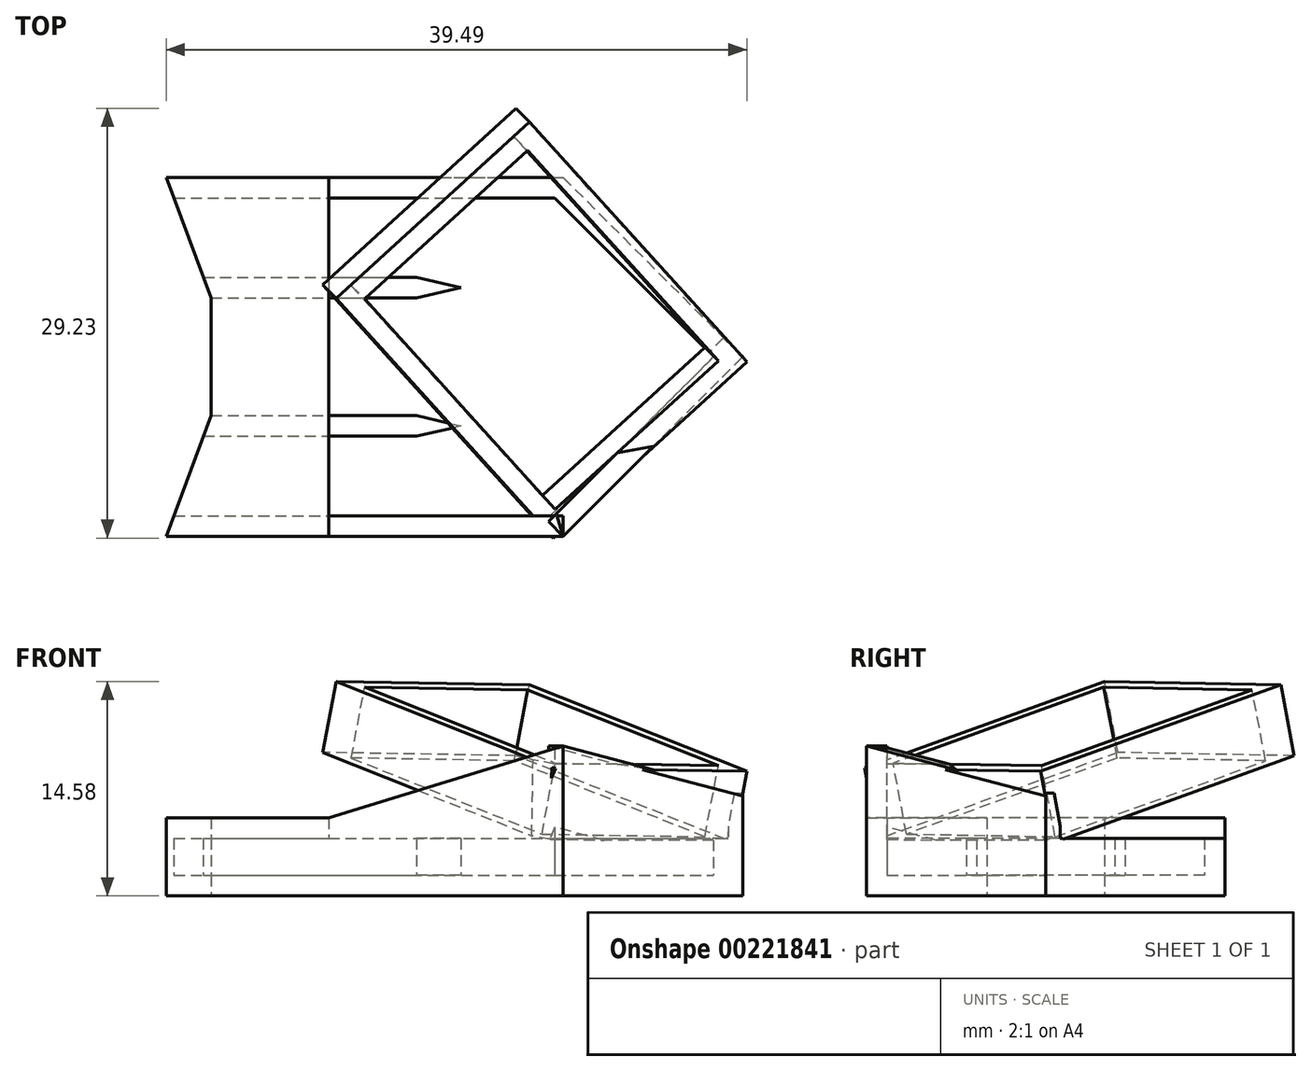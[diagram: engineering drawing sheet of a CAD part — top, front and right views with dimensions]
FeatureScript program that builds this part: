
annotation { "Feature Type Name" : "Feature", "Feature Type Description" : "" }
export const myFeature = defineFeature(function(context is Context, id is Id, definition is map)
    precondition{}
    {
        {
            var Q0;
            Q0=qCreatedBy(makeId("Top.planeOp"),FACE);
            var sketch = newSketch(context, id + "F0", { "sketchPlane" : qUnion([Q0])});
            skLineSegment(sketch, "E0", {"start": v(0, 12.2) * mm, "end": v(3.03, 4) * mm});
            skLineSegment(sketch, "E1", {"start": v(3.03, 4) * mm, "end": v(3.03, 0) * mm});
            skLineSegment(sketch, "E2", {"start": v(0, 12.2) * mm, "end": v(27, 12.2) * mm});
            skLineSegment(sketch, "E3", {"start": v(27, 12.2) * mm, "end": v(39.2, 0) * mm});
            skLineSegment(sketch, "E4.MirrorCS", {"start": v(0, -12.2) * mm, "end": v(3.03, -4) * mm});
            skLineSegment(sketch, "E5.MirrorCS", {"start": v(3.03, -4) * mm, "end": v(3.03, 0) * mm});
            skLineSegment(sketch, "E6.MirrorCS", {"start": v(27, -12.2) * mm, "end": v(39.2, 0) * mm});
            skLineSegment(sketch, "E7.MirrorCS", {"start": v(0, -12.2) * mm, "end": v(27, -12.2) * mm});
            skSolve(sketch);
        }
        {
            var Q0;
            Q0=makeQuery(id+"F0.imprint","IMPRINT",FACE,{"disambiguationData":[TD([[makeQuery(id+"F0.imprint","IMPRINT",EDGE,{"derivedFrom":sQuery(id+"F0.wireOp",EDGE,"E0")}),1.0]])]});
            extrude(context, id + "F1", {"entities" : qUnion([Q0]), "depth" : 1.4 * mm});
        }
        {
            var Q0;
            Q0=makeQuery(id+"F1.opExtrude","CAP_FACE",FACE,{"disambiguationData":[OSD([sQuery(id+"F0.wireOp",EDGE,"E0"),sQuery(id+"F0.wireOp",EDGE,"E1"),sQuery(id+"F0.wireOp",EDGE,"E2"),sQuery(id+"F0.wireOp",EDGE,"E3"),sQuery(id+"F0.wireOp",EDGE,"E4.MirrorCS"),sQuery(id+"F0.wireOp",EDGE,"E5.MirrorCS"),sQuery(id+"F0.wireOp",EDGE,"E6.MirrorCS"),sQuery(id+"F0.wireOp",EDGE,"E7.MirrorCS")])],"isStart":false});
            var sketch = newSketch(context, id + "F2", { "sketchPlane" : qUnion([Q0])});
            skLineSegment(sketch, "E8.0", {"start": v(0, -12.2) * mm, "end": v(3.03, -4) * mm});
            skLineSegment(sketch, "E9.0", {"start": v(0, 12.2) * mm, "end": v(3.03, 4) * mm});
            skLineSegment(sketch, "E10", {"start": v(3.03, -4) * mm, "end": v(17.03, -4) * mm});
            skLineSegment(sketch, "E11", {"start": v(2.51, -5.4) * mm, "end": v(17.03, -5.4) * mm});
            skLineSegment(sketch, "E12", {"start": v(17.03, -4) * mm, "end": v(17.03, -5.4) * mm, "construction": true});
            skLineSegment(sketch, "E13", {"start": v(17.03, -4) * mm, "end": v(20.03, -4.7) * mm});
            skPoint(sketch, "E13.endSnap0", {"position": v(17.03, -4.7) * mm});
            skLineSegment(sketch, "E14", {"start": v(20.03, -4.7) * mm, "end": v(17.03, -5.4) * mm});
            skLineSegment(sketch, "E15.MirrorCS", {"start": v(17.03, 4) * mm, "end": v(20.03, 4.7) * mm});
            skLineSegment(sketch, "E16.MirrorCS", {"start": v(20.03, 4.7) * mm, "end": v(17.03, 5.4) * mm});
            skLineSegment(sketch, "E17.MirrorCS", {"start": v(2.51, 5.4) * mm, "end": v(17.03, 5.4) * mm});
            skLineSegment(sketch, "E18.MirrorCS", {"start": v(3.03, 4) * mm, "end": v(17.03, 4) * mm});
            skLineSegment(sketch, "E19.0", {"start": v(0, -12.2) * mm, "end": v(27, -12.2) * mm});
            skLineSegment(sketch, "E20.0", {"start": v(27, -12.2) * mm, "end": v(39.2, 0) * mm});
            skLineSegment(sketch, "E21", {"start": v(0.52, -10.8) * mm, "end": v(26.42, -10.8) * mm});
            skLineSegment(sketch, "E22", {"start": v(26.42, -10.8) * mm, "end": v(37.22, 0) * mm});
            skLineSegment(sketch, "E23.MirrorCS", {"start": v(26.42, 10.8) * mm, "end": v(37.22, 0) * mm});
            skLineSegment(sketch, "E24.MirrorCS", {"start": v(0.52, 10.8) * mm, "end": v(26.42, 10.8) * mm});
            skLineSegment(sketch, "E25.MirrorCS", {"start": v(0, 12.2) * mm, "end": v(27, 12.2) * mm});
            skLineSegment(sketch, "E26.MirrorCS", {"start": v(27, 12.2) * mm, "end": v(39.2, 0) * mm});
            skSolve(sketch);
        }
        {
            var Q0;
            Q0 = qSketchRegion(id + "F2", true);
            extrude(context, id + "F3", {"entities" : qUnion([Q0]), "operationType" : NewBodyOperationType.ADD, "depth" : 2.5 * mm});
        }
        {
            var Q0;
            Q0=makeQuery(id+"F3.opExtrude","CAP_FACE",FACE,{"disambiguationData":[OSD([sQuery(id+"F2.wireOp",EDGE,"E8.0"),sQuery(id+"F2.wireOp",EDGE,"E10"),sQuery(id+"F2.wireOp",EDGE,"E11"),sQuery(id+"F2.wireOp",EDGE,"E13"),sQuery(id+"F2.wireOp",EDGE,"E14")])],"isStart":false});
            var sketch = newSketch(context, id + "F4", { "sketchPlane" : qUnion([Q0])});
            skLineSegment(sketch, "E27.0", {"start": v(0, 12.2) * mm, "end": v(2.51, 5.4) * mm});
            skLineSegment(sketch, "E28.0", {"start": v(0, 12.2) * mm, "end": v(11.03, 12.2) * mm});
            skLineSegment(sketch, "E29.0.0", {"start": v(2.51, 5.4) * mm, "end": v(3.03, 4) * mm});
            skLineSegment(sketch, "E30.0", {"start": v(3.03, 4) * mm, "end": v(3.03, -4) * mm});
            skLineSegment(sketch, "E31.0", {"start": v(0, -12.2) * mm, "end": v(2.51, -5.4) * mm});
            skLineSegment(sketch, "E32.0", {"start": v(0, -12.2) * mm, "end": v(11.03, -12.2) * mm});
            skLineSegment(sketch, "E33", {"start": v(11.03, 12.2) * mm, "end": v(11.03, -12.2) * mm});
            skPoint(sketch, "E29.0.3.end.orphan", {"position": v(17.03, 5.4) * mm});
            skPoint(sketch, "E29.0.2.end.orphan", {"position": v(20.03, 4.7) * mm});
            skPoint(sketch, "E34.orphan", {"position": v(17.03, 4) * mm});
            skPoint(sketch, "E35.0.3.end.orphan", {"position": v(17.03, -4) * mm});
            skPoint(sketch, "E35.0.2.end.orphan", {"position": v(20.03, -4.7) * mm});
            skPoint(sketch, "E35.0.2.start.orphan", {"position": v(17.03, -5.4) * mm});
            skLineSegment(sketch, "E36", {"start": v(3.03, -4) * mm, "end": v(2.51, -5.4) * mm});
            skSolve(sketch);
        }
        {
            var Q0;
            Q0=makeQuery(id+"F4.imprint","IMPRINT",FACE,{"disambiguationData":[TD([[makeQuery(id+"F4.imprint","IMPRINT",EDGE,{"derivedFrom":sQuery(id+"F4.wireOp",EDGE,"E27.0")}),1.0]])]});
            var Q1;
            {var subQ5=sQuery(id+"F4.wireOp",EDGE,"E36");Q1=makeQuery(id+"F4.imprint","IMPRINT",FACE,{"disambiguationData":[TD([[makeQuery(id+"F4.imprint","IMPRINT",EDGE,{"derivedFrom":subQ5}),-1.0]])]});}
            var Q2;
            {var subQ0=sQuery(id+"F4.wireOp",EDGE,"E31.0");Q2=makeQuery(id+"F4.imprint","IMPRINT",FACE,{"disambiguationData":[TD([[makeQuery(id+"F4.imprint","IMPRINT",EDGE,{"derivedFrom":subQ0}),-1.0]])]});}
            extrude(context, id + "F5", {"entities" : qUnion([Q0, Q1, Q2]), "operationType" : NewBodyOperationType.ADD, "depth" : 1.4 * mm});
        }
        {
            var Q0;
            Q0=makeQuery(id+"F5.boolean.opBoolean","MERGE",FACE,{"derivedFrom":[makeQuery(id+"F3.boolean.opBoolean","MERGE",FACE,{"derivedFrom":[makeQuery(id+"F1.opExtrude","SWEPT_FACE",FACE,{"disambiguationData":[OSD([sQuery(id+"F0.wireOp",EDGE,"E7.MirrorCS")])]}),makeQuery(id+"F3.opExtrude","SWEPT_FACE",FACE,{"disambiguationData":[OSD([sQuery(id+"F2.wireOp",EDGE,"E19.0")])]})]}),makeQuery(id+"F5.opExtrude","SWEPT_FACE",FACE,{"disambiguationData":[OSD([sQuery(id+"F4.wireOp",EDGE,"E32.0")])]})]});
            var sketch = newSketch(context, id + "F6", { "sketchPlane" : qUnion([Q0])});
            skLineSegment(sketch, "E37", {"start": v(11.03, 5.3) * mm, "end": v(27, 10.18) * mm});
            skLineSegment(sketch, "E38.0", {"start": v(11.03, 5.3) * mm, "end": v(11.03, 3.9) * mm});
            skLineSegment(sketch, "E39.0", {"start": v(11.03, 3.9) * mm, "end": v(27, 3.9) * mm});
            skLineSegment(sketch, "E40", {"start": v(27, 10.18) * mm, "end": v(27, 3.9) * mm});
            skSolve(sketch);
        }
        {
            var Q0;
            Q0 = qSketchRegion(id + "F6", true);
            var Q1;
            Q1=makeQuery(id+"F3.opExtrude","SWEPT_FACE",FACE,{"disambiguationData":[OSD([sQuery(id+"F2.wireOp",EDGE,"E21")])]});
            extrude(context, id + "F7", {"entities" : qUnion([Q0]), "operationType" : NewBodyOperationType.ADD, "endBound" : BoundingType.UP_TO_SURFACE, "oppositeDirection" : true, "endBoundEntityFace" : qUnion([Q1]), "depth" : 25 * mm});
        }
        {
            var Q0;
            Q0=makeQuery(id+"F3.boolean.opBoolean","MERGE",FACE,{"derivedFrom":[makeQuery(id+"F1.opExtrude","SWEPT_FACE",FACE,{"disambiguationData":[OSD([sQuery(id+"F0.wireOp",EDGE,"E6.MirrorCS")])]}),makeQuery(id+"F3.opExtrude","SWEPT_FACE",FACE,{"disambiguationData":[OSD([sQuery(id+"F2.wireOp",EDGE,"E20.0")])]})]});
            var sketch = newSketch(context, id + "F8", { "sketchPlane" : qUnion([Q0])});
            skLineSegment(sketch, "E41.0", {"start": v(10.47, 10.18) * mm, "end": v(10.47, 3.9) * mm});
            skLineSegment(sketch, "E42.0", {"start": v(10.47, 3.9) * mm, "end": v(27.72, 3.9) * mm});
            skLineSegment(sketch, "E43", {"start": v(10.47, 10.18) * mm, "end": v(27.72, 6.98) * mm});
            skLineSegment(sketch, "E44", {"start": v(27.72, 6.98) * mm, "end": v(27.72, 3.9) * mm});
            skSolve(sketch);
        }
        {
            var Q0;
            Q0 = qSketchRegion(id + "F8", true);
            extrude(context, id + "F9", {"entities" : qUnion([Q0]), "operationType" : NewBodyOperationType.ADD, "oppositeDirection" : true, "depth" : 1.4 * mm});
        }
        {
            var Q0;
            Q0=qCreatedBy(makeId("Top.planeOp"),FACE);
            var Q1;
            Q1=makeQuery(id+"F1.opExtrude","CAP_EDGE",EDGE,{"disambiguationData":[OSD([sQuery(id+"F0.wireOp",EDGE,"E6.MirrorCS")])],"isStart":true});
            cPlane(context, id + "F10", {"entities" : qUnion([Q0, Q1]), "cplaneType" : CPlaneType.LINE_ANGLE, "offset" : 25 * mm, "angle" : 15 * degree, "width" : 150 * mm, "height" : 150 * mm});
        }
        {
            var Q0;
            Q0=makeQuery(id+"F9.opExtrude","CAP_EDGE",EDGE,{"disambiguationData":[OSD([sQuery(id+"F8.wireOp",EDGE,"E43")])],"isStart":true});
            cPoint(context, id + "F11", {"entities" : qUnion([Q0]), "parameter" : 0.5});
        }
        {
            var Q0;
            Q0=qCreatedBy(id+"F10.planeOp",FACE);
            var Q1;
            Q1 = qCreatedBy(id + "F11" ,VERTEX);
            cPlane(context, id + "F12", {"entities" : qUnion([Q0, Q1]), "cplaneType" : CPlaneType.PLANE_POINT, "offset" : 25 * mm, "width" : 150 * mm, "height" : 150 * mm});
        }
        {
            var Q0;
            Q0=qCreatedBy(id+"F12.planeOp",FACE);
            var sketch = newSketch(context, id + "F13", { "sketchPlane" : qUnion([Q0])});
            skLineSegment(sketch, "E45.0", {"start": v(23.36, 9.12) * mm, "end": v(36.34, -2.27) * mm});
            skLineSegment(sketch, "E46", {"start": v(24.04, 8.52) * mm, "end": v(35.31, -1.37) * mm});
            skLineSegment(sketch, "E47", {"start": v(35.31, -1.37) * mm, "end": v(22.12, -16.4) * mm});
            skLineSegment(sketch, "E48", {"start": v(22.12, -16.4) * mm, "end": v(10.85, -6.5) * mm});
            skLineSegment(sketch, "E49", {"start": v(10.85, -6.5) * mm, "end": v(24.04, 8.52) * mm});
            skLineSegment(sketch, "E50.0", {"start": v(22.25, -18.38) * mm, "end": v(8.87, -6.64) * mm});
            skLineSegment(sketch, "E50.1", {"start": v(37.29, -1.24) * mm, "end": v(22.25, -18.38) * mm});
            skLineSegment(sketch, "E50.2", {"start": v(23.9, 10.5) * mm, "end": v(37.29, -1.24) * mm});
            skLineSegment(sketch, "E50.3", {"start": v(8.87, -6.64) * mm, "end": v(23.9, 10.5) * mm});
            skSolve(sketch);
        }
        {
            var Q0;
            Q0 = qSketchRegion(id + "F13", true);
            extrude(context, id + "F14", {"entities" : qUnion([Q0]), "operationType" : NewBodyOperationType.ADD, "depth" : 5 * mm});
        }
    });
